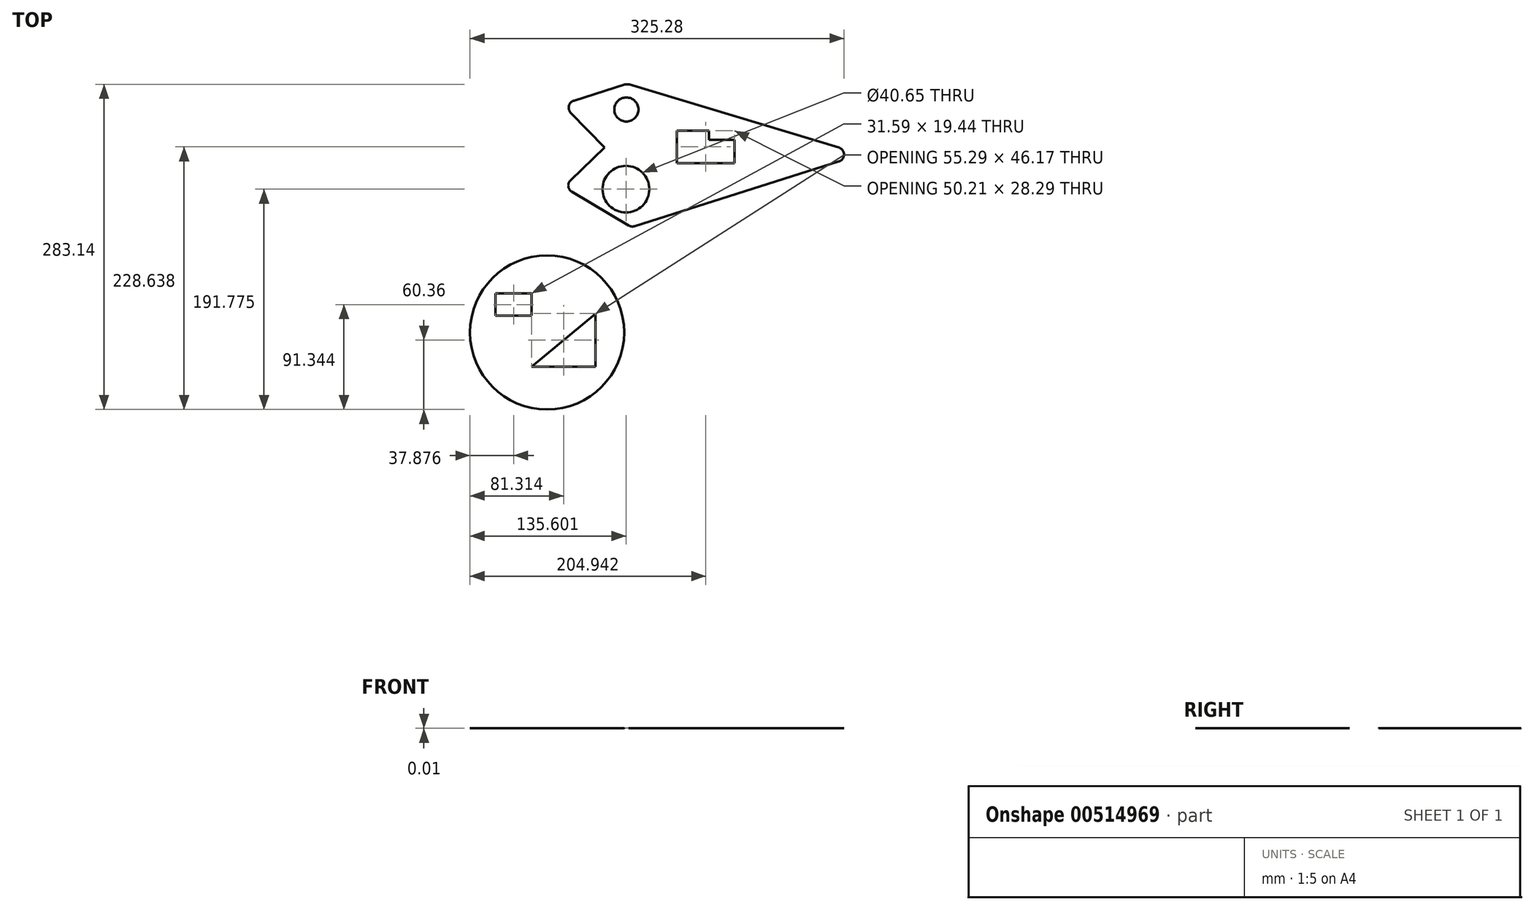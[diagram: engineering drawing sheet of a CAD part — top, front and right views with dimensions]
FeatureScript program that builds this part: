
annotation { "Feature Type Name" : "Feature", "Feature Type Description" : "" }
export const myFeature = defineFeature(function(context is Context, id is Id, definition is map)
    precondition{}
    {
        {
            var Q0;
            Q0=qCreatedBy(makeId("Top.planeOp"),FACE);
            var sketch = newSketch(context, id + "F0", { "sketchPlane" : qUnion([Q0])});
            skLineSegment(sketch, "E0", {"start": v(-53.53, 54.83) * mm, "end": v(128.57, -0.05) * mm});
            skLineSegment(sketch, "E1", {"start": v(128.66, -12.18) * mm, "end": v(-49.1, -68.48) * mm});
            skLineSegment(sketch, "E2", {"start": v(-54.25, -67.89) * mm, "end": v(-103.64, -38.52) * mm});
            skLineSegment(sketch, "E3", {"start": v(-104.8, -28.5) * mm, "end": v(-75.32, 0) * mm});
            skLineSegment(sketch, "E4", {"start": v(-75.32, 0) * mm, "end": v(-104.63, 30.33) * mm});
            skLineSegment(sketch, "E5", {"start": v(-101.96, 40.8) * mm, "end": v(-57.26, 54.81) * mm});
            skPoint(sketch, "E6.visualSharp", {"position": v(-111.78, 37.73) * mm});
            skArc(sketch, "E6.filletArc", {"start": v(-101.96, 40.8) * mm, "mid": v(-106.22, 36.31) * mm, "end": v(-104.63, 30.33) * mm});
            skPoint(sketch, "E7.visualSharp", {"position": v(-110.79, -34.27) * mm});
            skArc(sketch, "E7.filletArc", {"start": v(-104.8, -28.5) * mm, "mid": v(-106.7, -33.8) * mm, "end": v(-103.64, -38.52) * mm});
            skPoint(sketch, "E8.visualSharp", {"position": v(-51.8, -69.34) * mm});
            skArc(sketch, "E8.filletArc", {"start": v(-54.25, -67.89) * mm, "mid": v(-51.74, -68.74) * mm, "end": v(-49.1, -68.48) * mm});
            skPoint(sketch, "E9.visualSharp", {"position": v(-55.4, 55.4) * mm});
            skArc(sketch, "E9.filletArc", {"start": v(-53.53, 54.83) * mm, "mid": v(-55.4, 55.1) * mm, "end": v(-57.26, 54.81) * mm});
            skPoint(sketch, "E10.visualSharp", {"position": v(148.25, -5.98) * mm});
            skArc(sketch, "E10.filletArc", {"start": v(128.66, -12.18) * mm, "mid": v(133.1, -6.08) * mm, "end": v(128.57, -0.05) * mm});
            skCircle(sketch, "E11", {"center": v(-56.2, 33.08) * mm, "radius": 10.5 * mm});
            skCircle(sketch, "E12", {"center": v(-56.59, -36.26) * mm, "radius": 20.32 * mm});
            skLineSegment(sketch, "E13", {"start": v(-12.35, 14.75) * mm, "end": v(15.54, 14.75) * mm});
            skLineSegment(sketch, "E14", {"start": v(15.54, 14.75) * mm, "end": v(15.54, 6.77) * mm});
            skLineSegment(sketch, "E15", {"start": v(15.54, 6.77) * mm, "end": v(37.86, 6.77) * mm});
            skLineSegment(sketch, "E16", {"start": v(37.86, 6.77) * mm, "end": v(37.86, -13.55) * mm});
            skLineSegment(sketch, "E17", {"start": v(37.86, -13.55) * mm, "end": v(-12.35, -13.55) * mm});
            skLineSegment(sketch, "E18", {"start": v(-12.35, -13.55) * mm, "end": v(-12.35, 14.75) * mm});
            skSolve(sketch);
        }
        {
            var Q0;
            Q0=makeQuery(id+"F0.imprint","IMPRINT",FACE,{"disambiguationData":[TD([[makeQuery(id+"F0.imprint","IMPRINT",EDGE,{"derivedFrom":sQuery(id+"F0.wireOp",EDGE,"E0")}),-1.0]])]});
            extrude(context, id + "F1", {"entities" : qUnion([Q0]), "depth" : 3 / 203.2 * mm, "offsetDistance" : 25.4 * mm});
        }
        {
            var Q0;
            Q0=qCreatedBy(makeId("Top.planeOp"),FACE);
            var sketch = newSketch(context, id + "F2", { "sketchPlane" : qUnion([Q0])});
            skCircle(sketch, "E19", {"center": v(-125.15, -161) * mm, "radius": 67.04 * mm});
            skLineSegment(sketch, "E20.bottom", {"start": v(-170.11, -126.98) * mm, "end": v(-138.52, -126.98) * mm});
            skLineSegment(sketch, "E20.top", {"start": v(-170.11, -146.42) * mm, "end": v(-138.52, -146.42) * mm});
            skLineSegment(sketch, "E20.left", {"start": v(-170.11, -126.98) * mm, "end": v(-170.11, -146.42) * mm});
            skLineSegment(sketch, "E20.right", {"start": v(-138.52, -126.98) * mm, "end": v(-138.52, -146.42) * mm});
            skLineSegment(sketch, "E21", {"start": v(-83.23, -144.6) * mm, "end": v(-83.23, -190.77) * mm});
            skLineSegment(sketch, "E22", {"start": v(-83.23, -190.77) * mm, "end": v(-138.52, -190.77) * mm});
            skLineSegment(sketch, "E23", {"start": v(-138.52, -190.77) * mm, "end": v(-83.23, -144.6) * mm});
            skSolve(sketch);
        }
        {
            var Q0;
            Q0=makeQuery(id+"F2.imprint","IMPRINT",FACE,{"disambiguationData":[TD([[makeQuery(id+"F2.imprint","IMPRINT",EDGE,{"derivedFrom":sQuery(id+"F2.wireOp",EDGE,"E19")}),1.0]])]});
            extrude(context, id + "F3", {"entities" : qUnion([Q0]), "depth" : 3 / 203.2 * mm, "offsetDistance" : 25.4 * mm});
        }
    });
